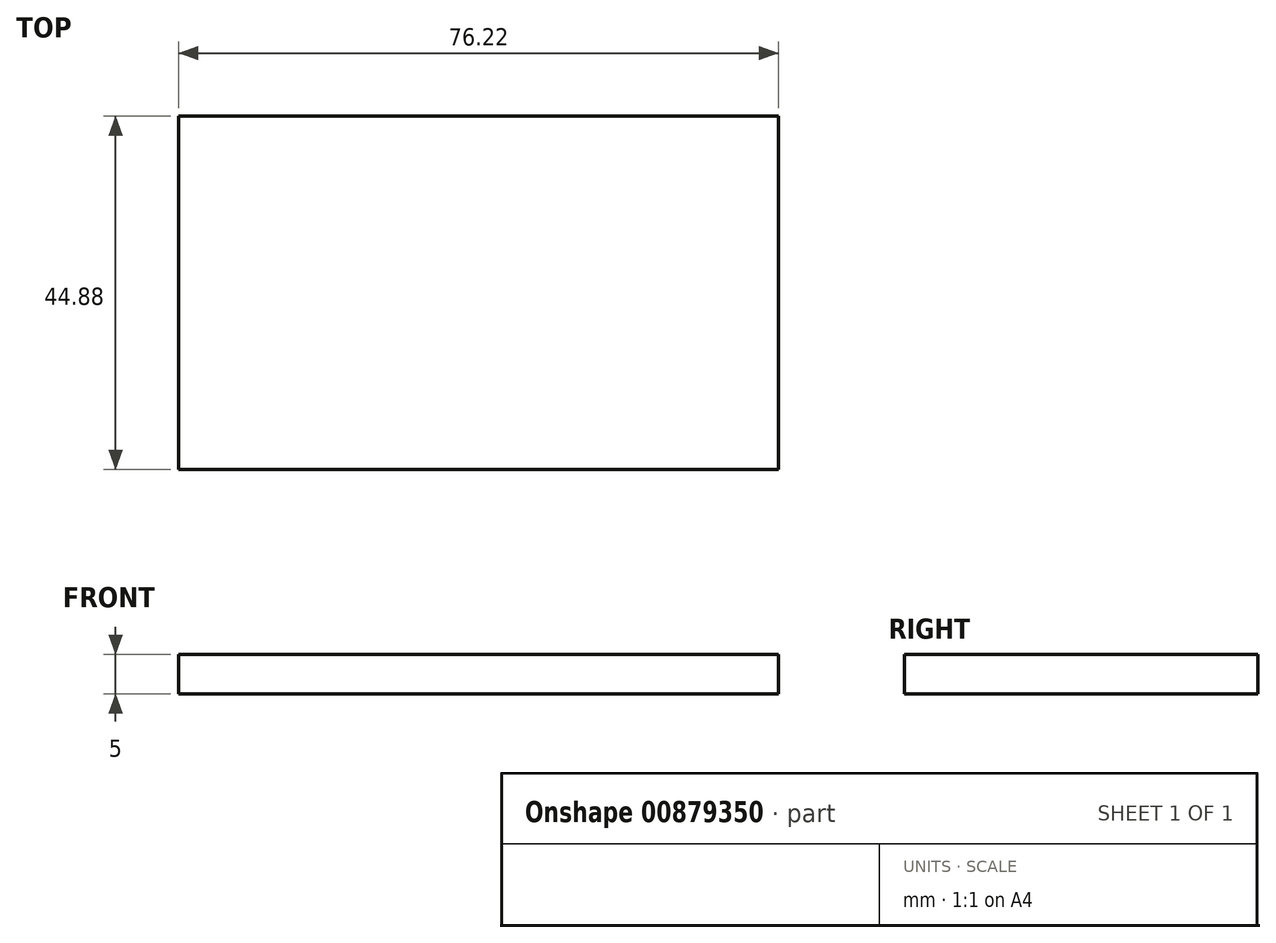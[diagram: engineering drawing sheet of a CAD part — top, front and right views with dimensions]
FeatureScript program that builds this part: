
annotation { "Feature Type Name" : "Feature", "Feature Type Description" : "" }
export const myFeature = defineFeature(function(context is Context, id is Id, definition is map)
    precondition{}
    {
        {
            var Q0;
            Q0=qCreatedBy(makeId("Top.planeOp"),FACE);
            var sketch = newSketch(context, id + "F0", { "sketchPlane" : qUnion([Q0])});
            skLineSegment(sketch, "E0.bottom", {"start": v(38.1, 22.44) * mm, "end": v(-38.1, 22.44) * mm});
            skLineSegment(sketch, "E0.top", {"start": v(38.1, -22.44) * mm, "end": v(-38.1, -22.44) * mm});
            skLineSegment(sketch, "E0.left", {"start": v(38.1, 22.44) * mm, "end": v(38.1, -22.44) * mm});
            skLineSegment(sketch, "E0.right", {"start": v(-38.1, 22.44) * mm, "end": v(-38.1, -22.44) * mm});
            skPoint(sketch, "E0.middle", {"position": v(0, 0) * mm});
            skSolve(sketch);
        }
        {
            var Q0;
            Q0=makeQuery(id+"F0.imprint","IMPRINT",FACE,{"disambiguationData":[TD([[makeQuery(id+"F0.imprint","IMPRINT",EDGE,{"derivedFrom":sQuery(id+"F0.wireOp",EDGE,"E0.bottom")}),1.0]])]});
            extrude(context, id + "F1", {"entities" : qUnion([Q0]), "depth" : 5 * mm, "offsetDistance" : 25 * mm});
        }
    });
